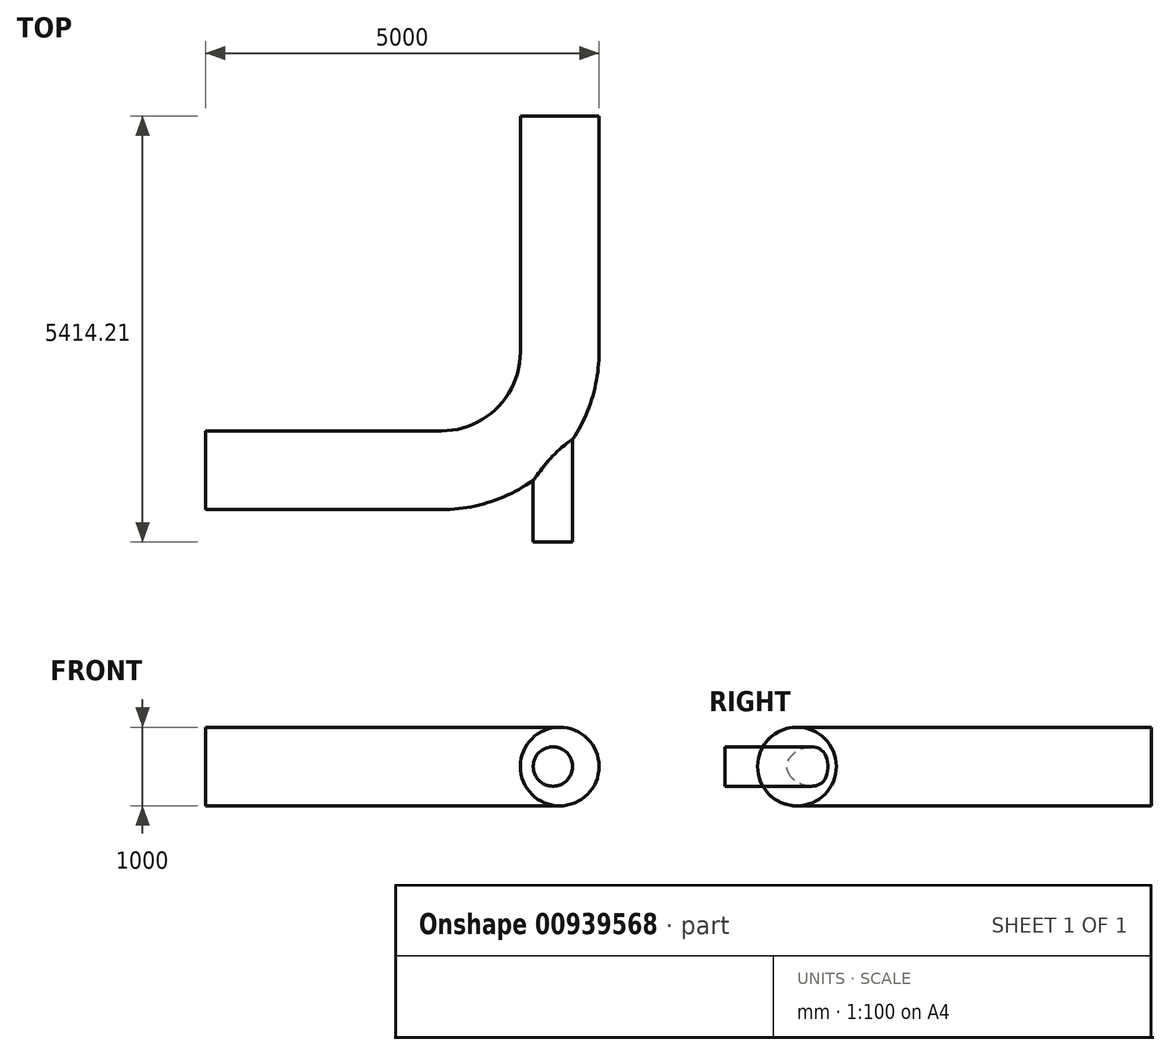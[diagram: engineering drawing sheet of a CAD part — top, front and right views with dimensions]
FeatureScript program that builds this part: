
annotation { "Feature Type Name" : "Feature", "Feature Type Description" : "" }
export const myFeature = defineFeature(function(context is Context, id is Id, definition is map)
    precondition{}
    {
        {
            var Q0;
            Q0=qCreatedBy(makeId("Top.planeOp"),FACE);
            var sketch = newSketch(context, id + "F0", { "sketchPlane" : qUnion([Q0])});
            skLineSegment(sketch, "E0", {"start": v(0, 0) * mm, "end": v(3000, 0) * mm});
            skArc(sketch, "E1", {"start": v(3000, 0) * mm, "mid": v(4060.66, 439.34) * mm, "end": v(4500, 1500) * mm});
            skLineSegment(sketch, "E2", {"start": v(4500, 1500) * mm, "end": v(4500, 4500) * mm});
            skArc(sketch, "E3.0", {"start": v(3000, -500) * mm, "mid": v(4414.21, 85.79) * mm, "end": v(5000, 1500) * mm, "construction": true});
            skLineSegment(sketch, "E4", {"start": v(4500, 1500) * mm, "end": v(5000, 1500) * mm, "construction": true});
            skLineSegment(sketch, "E5", {"start": v(4414.21, 85.79) * mm, "end": v(4414.21, -914.21) * mm, "construction": true});
            skSolve(sketch);
        }
        {
            var Q0;
            Q0=qCreatedBy(makeId("Right.planeOp"),FACE);
            var sketch = newSketch(context, id + "F1", { "sketchPlane" : qUnion([Q0])});
            skCircle(sketch, "E6", {"center": v(0, 0) * mm, "radius": 500 * mm});
            skSolve(sketch);
        }
        {
            var Q0;
            Q0=makeQuery(id+"F1.imprint","IMPRINT",FACE,{"disambiguationData":[TD([[makeQuery(id+"F1.imprint","IMPRINT",EDGE,{"derivedFrom":sQuery(id+"F1.wireOp",EDGE,"E6")}),1.0]])]});
            var Q1;
            Q1=sQuery(id+"F1.wireOp",EDGE,"E6");
            var Q2;
            Q2=sQuery(id+"F0.wireOp",EDGE,"E0");
            var Q3;
            Q3=sQuery(id+"F0.wireOp",EDGE,"E1");
            var Q4;
            Q4=sQuery(id+"F0.wireOp",EDGE,"E2");
            sweep(context, id + "F2", {"profiles" : qUnion([Q0]), "surfaceProfiles" : qUnion([Q1]), "path" : qUnion([Q2, Q3, Q4])});
        }
        {
            var Q0;
            Q0=qCreatedBy(makeId("Front.planeOp"),FACE);
            var Q1;
            Q1=sQuery(id+"F0.wireOp",VERTEX,"E5.end");
            cPlane(context, id + "F3", {"entities" : qUnion([Q0, Q1]), "cplaneType" : CPlaneType.PLANE_POINT, "offset" : 25.4 * mm, "width" : 152.4 * mm, "height" : 152.4 * mm});
        }
        {
            var Q0;
            Q0=qCreatedBy(id+"F3.planeOp",FACE);
            var sketch = newSketch(context, id + "F4", { "sketchPlane" : qUnion([Q0])});
            skPoint(sketch, "E7.0", {"position": v(4414.21, 0) * mm});
            skCircle(sketch, "E8", {"center": v(4414.21, 0) * mm, "radius": 250 * mm});
            skSolve(sketch);
        }
        {
            var Q0;
            Q0=makeQuery(id+"F4.imprint","IMPRINT",FACE,{"disambiguationData":[TD([[makeQuery(id+"F4.imprint","IMPRINT",EDGE,{"derivedFrom":sQuery(id+"F4.wireOp",EDGE,"E8")}),1.0]])]});
            extrude(context, id + "F5", {"entities" : qUnion([Q0]), "operationType" : NewBodyOperationType.ADD, "endBound" : BoundingType.UP_TO_NEXT, "oppositeDirection" : true, "depth" : 25.4 * mm, "offsetDistance" : 25.4 * mm});
        }
    });
